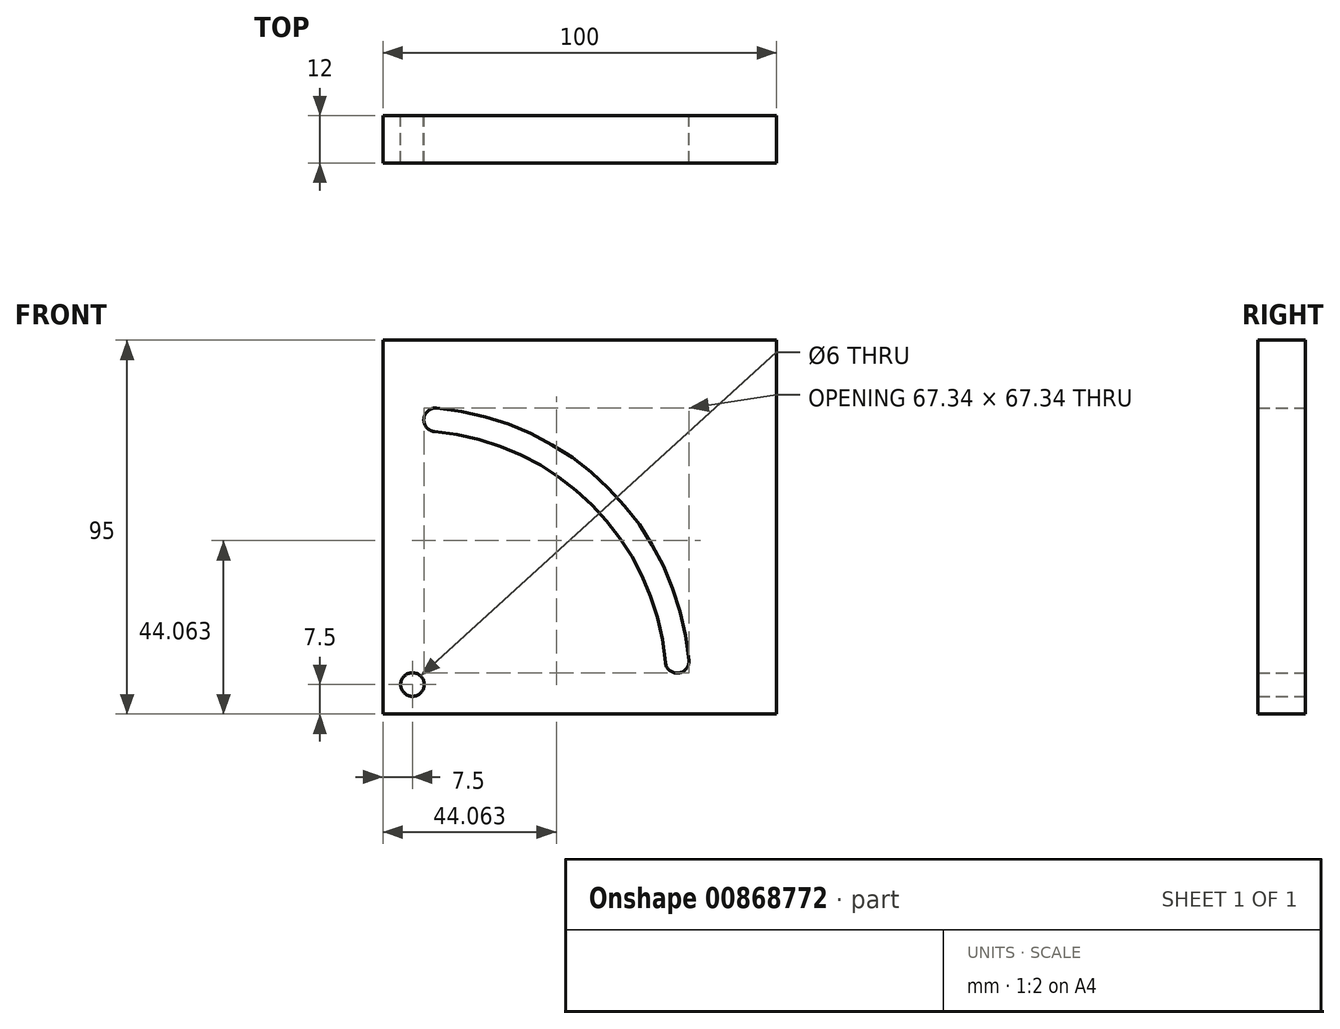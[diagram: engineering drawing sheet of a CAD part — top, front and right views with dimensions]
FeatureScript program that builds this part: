
annotation { "Feature Type Name" : "Feature", "Feature Type Description" : "" }
export const myFeature = defineFeature(function(context is Context, id is Id, definition is map)
    precondition{}
    {
        {
            var Q0;
            Q0=qCreatedBy(makeId("Front.planeOp"),FACE);
            var sketch = newSketch(context, id + "F0", { "sketchPlane" : qUnion([Q0])});
            skCircle(sketch, "E0", {"center": v(0, 0) * mm, "radius": 3 * mm});
            skLineSegment(sketch, "E1.bottom", {"start": v(-7.5, -7.5) * mm, "end": v(92.5, -7.5) * mm});
            skLineSegment(sketch, "E1.top", {"start": v(-7.5, 87.5) * mm, "end": v(92.5, 87.5) * mm});
            skLineSegment(sketch, "E1.left", {"start": v(-7.5, -7.5) * mm, "end": v(-7.5, 87.5) * mm});
            skLineSegment(sketch, "E1.right", {"start": v(92.5, -7.5) * mm, "end": v(92.5, 87.5) * mm});
            skArc(sketch, "E2", {"start": v(6.14, 70.23) * mm, "mid": v(49.85, 49.85) * mm, "end": v(70.23, 6.14) * mm});
            skArc(sketch, "E3", {"start": v(5.88, 67.24) * mm, "mid": v(47.73, 47.73) * mm, "end": v(67.24, 5.88) * mm, "construction": true});
            skLineSegment(sketch, "E4", {"start": v(0, 0) * mm, "end": v(70.23, 6.14) * mm, "construction": true});
            skLineSegment(sketch, "E5", {"start": v(0, 0) * mm, "end": v(6.14, 70.23) * mm, "construction": true});
            skPoint(sketch, "E6.orphan", {"position": v(0, 70.5) * mm});
            skPoint(sketch, "E7.orphan", {"position": v(0, 67.5) * mm});
            skArc(sketch, "E8", {"start": v(6.14, 70.23) * mm, "mid": v(2.9, 67.5) * mm, "end": v(5.62, 64.25) * mm});
            skArc(sketch, "E9", {"start": v(64.25, 5.62) * mm, "mid": v(67.5, 2.9) * mm, "end": v(70.23, 6.14) * mm});
            skArc(sketch, "E10", {"start": v(5.62, 64.25) * mm, "mid": v(45.6, 45.6) * mm, "end": v(64.25, 5.62) * mm});
            skSolve(sketch);
        }
        {
            var Q0;
            Q0=makeQuery(id+"F0.imprint","IMPRINT",FACE,{"disambiguationData":[TD([[makeQuery(id+"F0.imprint","IMPRINT",EDGE,{"derivedFrom":sQuery(id+"F0.wireOp",EDGE,"E0")}),-1.0]])]});
            extrude(context, id + "F1", {"entities" : qUnion([Q0]), "depth" : 12 * mm, "offsetDistance" : 25 * mm, "symmetric" : true});
        }
    });
